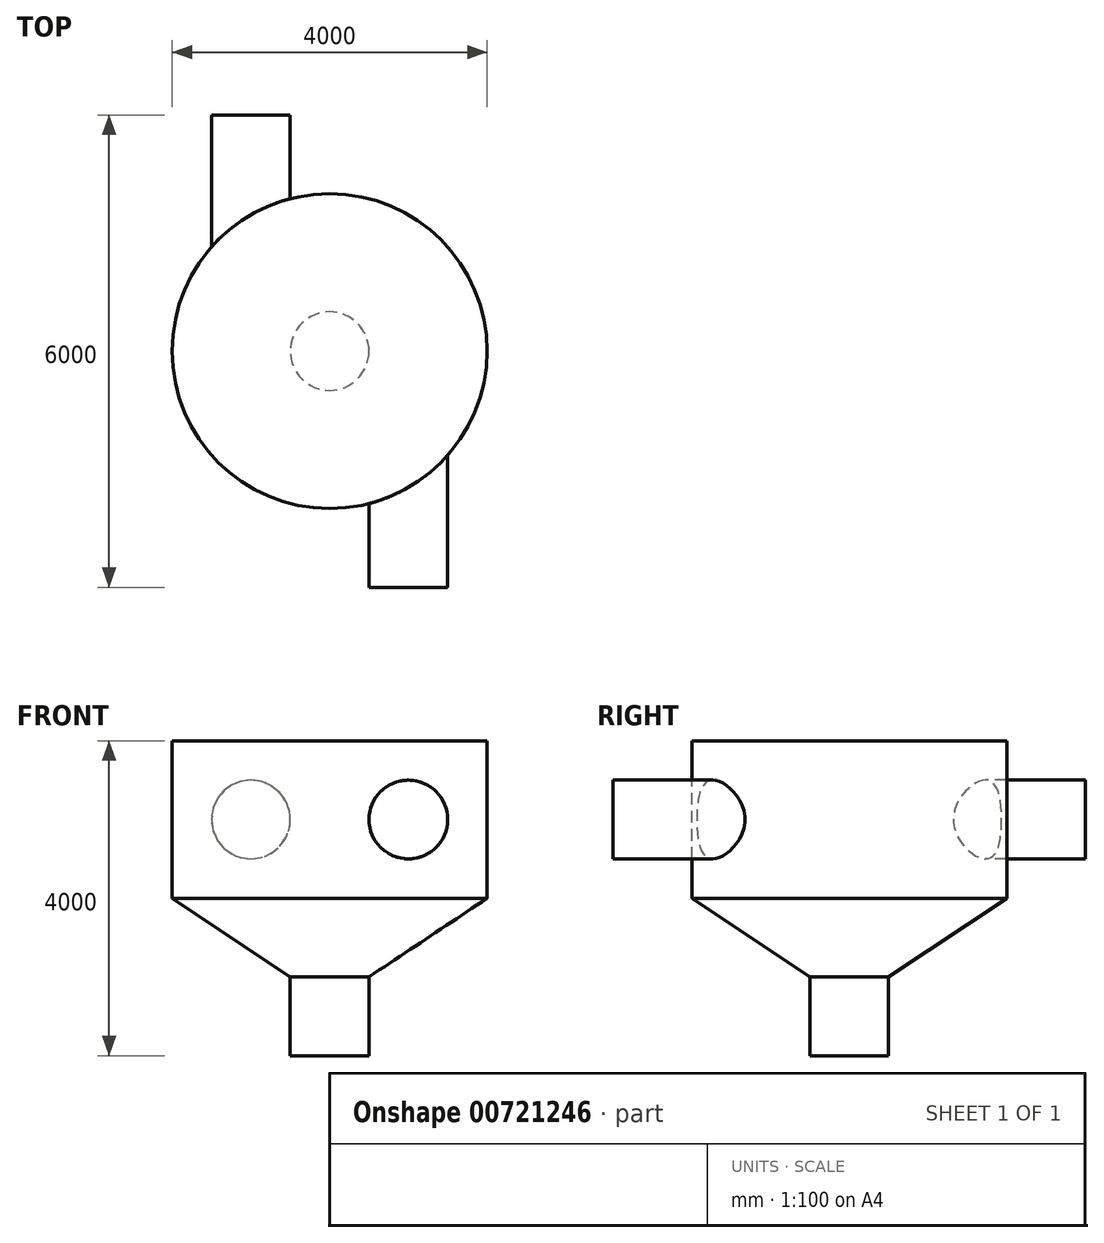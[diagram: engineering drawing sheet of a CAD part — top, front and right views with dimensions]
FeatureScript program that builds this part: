
annotation { "Feature Type Name" : "Feature", "Feature Type Description" : "" }
export const myFeature = defineFeature(function(context is Context, id is Id, definition is map)
    precondition{}
    {
        {
            var Q0;
            Q0=qCreatedBy(makeId("Front.planeOp"),FACE);
            var sketch = newSketch(context, id + "F0", { "sketchPlane" : qUnion([Q0])});
            skLineSegment(sketch, "E0", {"start": v(0, 0) * mm, "end": v(500, 0) * mm});
            skLineSegment(sketch, "E1", {"start": v(500, 0) * mm, "end": v(500, 1000) * mm});
            skLineSegment(sketch, "E2", {"start": v(500, 1000) * mm, "end": v(2000, 2000) * mm});
            skLineSegment(sketch, "E3", {"start": v(2000, 2000) * mm, "end": v(2000, 4000) * mm});
            skLineSegment(sketch, "E4", {"start": v(2000, 4000) * mm, "end": v(0, 4000) * mm});
            skLineSegment(sketch, "E5", {"start": v(0, 4000) * mm, "end": v(0, 0) * mm});
            skSolve(sketch);
        }
        {
            var Q0;
            Q0=qSketchRegion(id+"F0",true);
            var Q1;
            Q1=sQuery(id+"F0.wireOp",EDGE,"E5");
            revolve(context, id + "F1", {"entities" : qUnion([Q0]), "axis" : qUnion([Q1]), "revolveType" : RevolveType.FULL, "surfaceOperationType" : NewSurfaceOperationType.NEW});
        }
        {
            var Q0;
            Q0=qCreatedBy(makeId("Front.planeOp"),FACE);
            var sketch = newSketch(context, id + "F2", { "sketchPlane" : qUnion([Q0])});
            skCircle(sketch, "E6", {"center": v(1000, 3000) * mm, "radius": 500 * mm});
            skSolve(sketch);
        }
        {
            var Q0;
            Q0=qSketchRegion(id+"F2",true);
            extrude(context, id + "F3", {"entities" : qUnion([Q0]), "operationType" : NewBodyOperationType.ADD, "depth" : 3000 * mm});
        }
        {
            var Q0;
            Q0=qCreatedBy(makeId("Front.planeOp"),FACE);
            var sketch = newSketch(context, id + "F4", { "sketchPlane" : qUnion([Q0])});
            skCircle(sketch, "E7", {"center": v(-1000, 3000) * mm, "radius": 500 * mm});
            skSolve(sketch);
        }
        {
            var Q0;
            Q0=qSketchRegion(id+"F4",true);
            extrude(context, id + "F5", {"entities" : qUnion([Q0]), "operationType" : NewBodyOperationType.ADD, "oppositeDirection" : true, "depth" : 3000 * mm, "offsetDistance" : 25 * mm});
        }
    });
